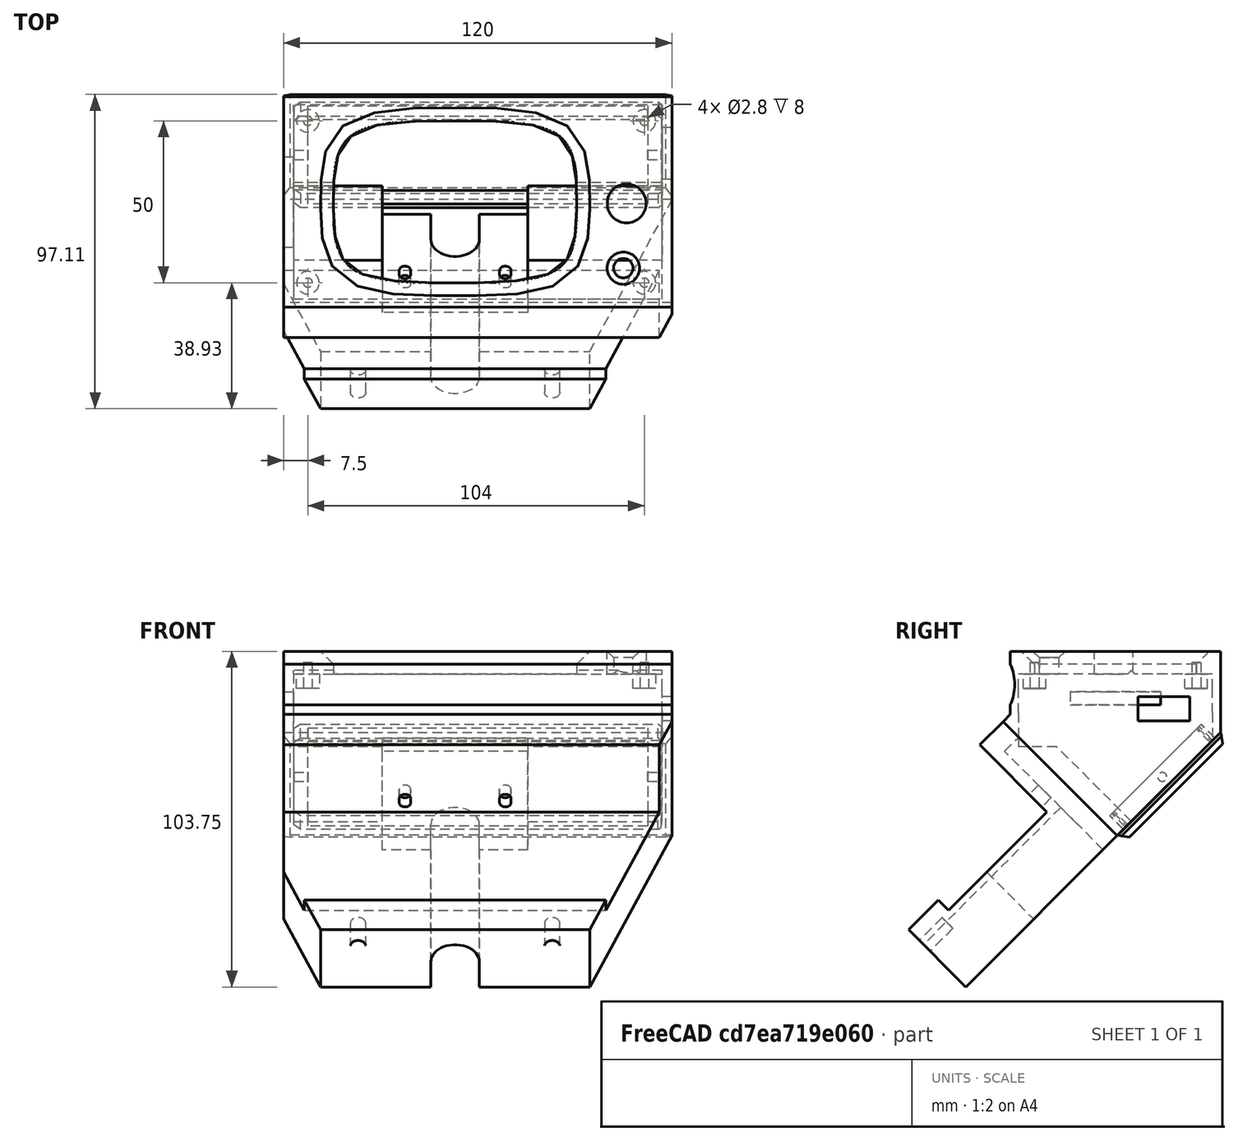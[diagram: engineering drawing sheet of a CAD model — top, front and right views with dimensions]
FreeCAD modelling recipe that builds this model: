
FCSTD DOCUMENT  (FreeCAD 0.19R)
Label: ScreenBezel2
License: All rights reserved
LicenseURL: http://en.wikipedia.org/wiki/All_rights_reserved
objects: Sketcher::SketchObject×24, PartDesign::Pocket×19, PartDesign::Chamfer×7, PartDesign::Pad×5, PartDesign::Body×2, PartDesign::Mirrored×1, Mesh::Feature×1
note: 89 computed .brp shape members not serialized (recipe doc carries the construction recipe); baked Part::Feature solids carry a one-line shape summary decoded from their .brp

FEATURE [Sketcher::SketchObject] Sketch
  FullyConstrained = true
  MapMode = 5
  Support = -> [XY_Plane]
  sketch-geometry (30):
    g0: LineSegment StartX=-53 StartY=32.5 StartZ=0 EndX=67 EndY=32.5 EndZ=0
    g1: LineSegment StartX=67 StartY=32.5 StartZ=0 EndX=67 EndY=-32.5 EndZ=0
    g2: LineSegment StartX=67 StartY=-32.5 StartZ=0 EndX=-53 EndY=-32.5 EndZ=0
    g3: LineSegment StartX=-53 StartY=-32.5 StartZ=0 EndX=-53 EndY=32.5 EndZ=0
    g4: LineSegment StartX=-37 StartY=24.5 StartZ=0 EndX=37 EndY=24.5 EndZ=0
    g5: LineSegment StartX=37 StartY=24.5 StartZ=0 EndX=37 EndY=-24.5 EndZ=0
    g6: LineSegment StartX=37 StartY=-24.5 StartZ=0 EndX=-37 EndY=-24.5 EndZ=0
    g7: LineSegment StartX=-37 StartY=-24.5 StartZ=0 EndX=-37 EndY=24.5 EndZ=0
    g8: LineSegment StartX=-37.7408 StartY=25.116 StartZ=0 EndX=37.7408 EndY=25.116 EndZ=0
    g9: LineSegment StartX=37.7408 StartY=25.116 StartZ=0 EndX=37.7408 EndY=-25.116 EndZ=0
    g10: LineSegment StartX=37.7408 StartY=-25.116 StartZ=0 EndX=-37.7408 EndY=-25.116 EndZ=0
    g11: LineSegment StartX=-37.7408 StartY=-25.116 StartZ=0 EndX=-37.7408 EndY=25.116 EndZ=0
    g12-g19: Circle x8 (B-spline internal-alignment scaffolding for g20; pole/knot coordinates omitted)
    g20: BSplineCurve PolesCount=8 KnotsCount=9 Degree=3 IsPeriodic=1
    g21-g29: GeomPoint x9 (B-spline internal-alignment scaffolding for g20; pole/knot coordinates omitted)
  constraints (53):
    c: Coincident(g0,g1)
    c: Coincident(g1,g2)
    c: Coincident(g2,g3)
    c: Coincident(g3,g0)
    c: Horizontal(g0)
    c: Horizontal(g2)
    c: Vertical(g1)
    c: Vertical(g3)
    c: Coincident(g4,g5)
    c: Coincident(g5,g6)
    c: Coincident(g6,g7)
    c: Coincident(g7,g4)
    c: Horizontal(g4)
    c: Vertical(g7)
    c: Distance(g5) = 49
    c: Distance(g4,g3) = 16
    c: Distance(g0,g5) = 30
    c: Distance(g6,g2) = 8
    c: Distance(g4,g0) = 8
    c: Distance(g6) = 74
    c: Symmetric(g5,g6,g-2)
    c: Symmetric(g5,g4,g-1)
    c: Coincident(g8,g9)
    c: Coincident(g9,g10)
    c: Coincident(g10,g11)
    c: Coincident(g11,g8)
    c: Horizontal(g8)
    c: Horizontal(g10)
    c: Vertical(g9)
    c: Vertical(g11)
    c: Symmetric(g9,g8,g-1)
    c: Weight(g12) = 1
    c: Equal(g12,g13)
    c: Equal(g12,g14)
    c: Equal(g12,g15)
    c: PointOnObject(g15,g-1)
    c: Equal(g12,g16)
    c: Equal(g12,g17)
    c: PointOnObject(g17,g-2)
    c: Equal(g12,g18)
    c: Equal(g12,g19)
    c: InternalAlignment(g12-g19 -> g20) x8
    c: InternalAlignment(g21-g29 -> g20) x9
    c: Coincident(g8,g12)
    c: Coincident(g14,g8)
    c: Coincident(g16,g10)
    c: Coincident(g18,g9)
    c: Distance(g19,g5) = 0.5
    c: Symmetric(g19,g15,g-2)
    c: Distance(g17,g6) = 0.5
    c: Symmetric(g17,g13,g-1)
    c: DistanceX(g8) = 37.7408
    c: DistanceY(g8) = 25.116
FEATURE [PartDesign::Pad] Pad
  Direction = (1,1,1)
  Length = 25
  Length2 = 100
  Profile = -> Sketch
  Type = 0
FEATURE [Sketcher::SketchObject] Sketch004  label="knob"
  FullyConstrained = false
  MapMode = 5
  Placement = pos=(0,0,0) rot=(1,0,0;3.14159rad)
  sketch-geometry (1):
    g0: Circle CenterX=52 CenterY=20.5 CenterZ=0 NormalX=0 NormalY=0 NormalZ=1 AngleXU=0 Radius=3
  constraints (1):
    c: Diameter(g0) = 6
FEATURE [PartDesign::Pocket] Pocket001
  BaseFeature = -> Pad
  Length = 5
  Length2 = 100
  Profile = -> Sketch004
  Type = 1
FEATURE [Sketcher::SketchObject] Sketch001  label="knob001"
  FullyConstrained = false
  MapMode = 5
  Placement = pos=(0,0,25) rot=(0,0,1;0rad)
  Support = -> [Pocket001]
  sketch-geometry (1):
    g0: Circle CenterX=53 CenterY=-0.5 CenterZ=0 NormalX=0 NormalY=0 NormalZ=1 AngleXU=0 Radius=6
  constraints (2):
    c: Diameter(g0) = 12
    c: DistanceY(g0) = -0.5
FEATURE [PartDesign::Pocket] Pocket
  BaseFeature = -> Pocket001
  Length = 5
  Length2 = 100
  Profile = -> Sketch001
  Type = 1
FEATURE [Sketcher::SketchObject] Sketch005  label="MainPCBPocket"
  FullyConstrained = true
  MapMode = 5
  Placement = pos=(0,0,0) rot=(1,0,0;3.14159rad)
  Support = -> [Pocket]
  sketch-geometry (4):
    g0: LineSegment StartX=-50 StartY=30 StartZ=0 EndX=64 EndY=30 EndZ=0
    g1: LineSegment StartX=64 StartY=30 StartZ=0 EndX=64 EndY=-30 EndZ=0
    g2: LineSegment StartX=64 StartY=-30 StartZ=0 EndX=-50 EndY=-30 EndZ=0
    g3: LineSegment StartX=-50 StartY=-30 StartZ=0 EndX=-50 EndY=30 EndZ=0
  constraints (11):
    c: Coincident(g0,g1)
    c: Coincident(g1,g2)
    c: Coincident(g2,g3)
    c: Coincident(g3,g0)
    c: Horizontal(g0)
    c: Horizontal(g2)
    c: Vertical(g1)
    c: Symmetric(g2,g0,g-1)
    c: DistanceX(g0) = -50
    c: DistanceY(g0) = 30
    c: DistanceX(g1) = 64
FEATURE [PartDesign::Pocket] Pocket002
  BaseFeature = -> Pocket
  Length = 18
  Length2 = 100
  Profile = -> Sketch005
  Type = 0
FEATURE [PartDesign::Chamfer] Chamfer
  Angle = 45
  Base = -> Pocket002 [Edge19]
  BaseFeature = -> Pocket002
  ChamferType = 0
  FlipDirection = false
  Size = 4
  Size2 = 1
  SupportTransform = false
FEATURE [Sketcher::SketchObject] Sketch006  label="standofs"
  FullyConstrained = true
  MapMode = 5
  Placement = pos=(0,0,18) rot=(1,0,0;3.14159rad)
  Support = -> [Chamfer]
  sketch-geometry (4):
    g0: Circle CenterX=-45.5 CenterY=25 CenterZ=0 NormalX=0 NormalY=0 NormalZ=1 AngleXU=0 Radius=3.5
    g1: Circle CenterX=-45.5 CenterY=-25 CenterZ=0 NormalX=0 NormalY=0 NormalZ=1 AngleXU=0 Radius=3.5
    g2: Circle CenterX=58.5 CenterY=-25 CenterZ=0 NormalX=0 NormalY=0 NormalZ=1 AngleXU=0 Radius=3.5
    g3: Circle CenterX=58.5 CenterY=25 CenterZ=0 NormalX=0 NormalY=0 NormalZ=1 AngleXU=0 Radius=3.5
  constraints (10):
    c: Diameter(g0) = 7
    c: Equal(g0,g1)
    c: Equal(g0,g3)
    c: Equal(g0,g2)
    c: Symmetric(g1,g0,g-1)
    c: Symmetric(g2,g3,g-1)
    c: Distance(g3,g2) = 50
    c: Distance(g1,g0) = 50
    c: Distance(g3,g0) = 104
    c: DistanceX(g0) = -45.5
FEATURE [PartDesign::Pad] Pad001
  BaseFeature = -> Chamfer
  Direction = (1,1,1)
  Length = 4.5
  Length2 = 100
  Profile = -> Sketch006
  Type = 0
FEATURE [Sketcher::SketchObject] Sketch007  label="holes"
  FullyConstrained = true
  MapMode = 5
  Placement = pos=(0,0,13.5) rot=(1,0,0;3.14159rad)
  Support = -> [Pad001]
  sketch-geometry (4):
    g0: Circle CenterX=-45.5 CenterY=25 CenterZ=0 NormalX=0 NormalY=0 NormalZ=1 AngleXU=0 Radius=1.4
    g1: Circle CenterX=58.5 CenterY=25 CenterZ=0 NormalX=0 NormalY=0 NormalZ=1 AngleXU=0 Radius=1.4
    g2: Circle CenterX=58.5 CenterY=-25 CenterZ=0 NormalX=0 NormalY=0 NormalZ=1 AngleXU=0 Radius=1.4
    g3: Circle CenterX=-45.5 CenterY=-25 CenterZ=0 NormalX=0 NormalY=0 NormalZ=1 AngleXU=0 Radius=1.4
  constraints (10):
    c: Distance(g3,g2) = 104
    c: Distance(g3,g0) = 50
    c: Symmetric(g3,g0,g-1)
    c: Symmetric(g2,g1,g-1)
    c: Diameter(g1) = 2.8
    c: Equal(g1,g2)
    c: Equal(g1,g3)
    c: Equal(g1,g0)
    c: DistanceX(g0) = -45.5
    c: Distance(g1,g2) = 50
FEATURE [PartDesign::Pocket] Pocket003
  BaseFeature = -> Pad001
  Length = 8
  Length2 = 100
  Profile = -> Sketch007
  Type = 0
FEATURE [Sketcher::SketchObject] Sketch008  label="USBhole"
  ExternalGeometry = -> [Pocket003]
  FullyConstrained = true
  MapMode = 5
  Placement = pos=(67,0,0) rot=(0.57735,0.57735,0.57735;2.0944rad)
  Support = -> [Pocket003]
  sketch-geometry (4):
    g0: LineSegment StartX=7 StartY=6.5 StartZ=0 EndX=23 EndY=6.5 EndZ=0
    g1: LineSegment StartX=23 StartY=6.5 StartZ=0 EndX=23 EndY=0 EndZ=0
    g2: LineSegment StartX=23 StartY=0 StartZ=0 EndX=7 EndY=0 EndZ=0
    g3: LineSegment StartX=7 StartY=0 StartZ=0 EndX=7 EndY=6.5 EndZ=0
  constraints (12):
    c: Coincident(g0,g1)
    c: Coincident(g1,g2)
    c: Coincident(g2,g3)
    c: Coincident(g3,g0)
    c: Horizontal(g0)
    c: Horizontal(g2)
    c: Vertical(g1)
    c: Vertical(g3)
    c: Distance(g-3,g0) = 7
    c: Distance(g0) = 16
    c: Distance(g0,g-4) = 7
    c: PointOnObject(g1,g-1)
FEATURE [PartDesign::Pocket] Pocket004
  BaseFeature = -> Pocket003
  Length = 9
  Length2 = 100
  Profile = -> Sketch008
  Type = 0
FEATURE [Sketcher::SketchObject] Sketch009  label="SDHole"
  ExternalGeometry = -> [Pocket004]
  FullyConstrained = true
  MapMode = 5
  Placement = pos=(-53,0,0) rot=(0.57735,-0.57735,-0.57735;2.0944rad)
  Support = -> [Pocket004]
  sketch-geometry (4):
    g0: LineSegment StartX=-14 StartY=12.5 StartZ=0 EndX=14 EndY=12.5 EndZ=0
    g1: LineSegment StartX=14 StartY=12.5 StartZ=0 EndX=14 EndY=8.5 EndZ=0
    g2: LineSegment StartX=14 StartY=8.5 StartZ=0 EndX=-14 EndY=8.5 EndZ=0
    g3: LineSegment StartX=-14 StartY=8.5 StartZ=0 EndX=-14 EndY=12.5 EndZ=0
  constraints (11):
    c: Coincident(g0,g1)
    c: Coincident(g1,g2)
    c: Coincident(g2,g3)
    c: Coincident(g3,g0)
    c: Horizontal(g0)
    c: Vertical(g1)
    c: Vertical(g3)
    c: Distance(g0,g-3) = 1
    c: Distance(g1) = 4
    c: Symmetric(g1,g2,g-2)
    c: Distance(g2) = 28
FEATURE [PartDesign::Pocket] Pocket005
  BaseFeature = -> Pocket004
  Length = 5
  Length2 = 100
  Profile = -> Sketch009
  Type = 0
FEATURE [Sketcher::SketchObject] Sketch010  label="TowerProper"
  FullyConstrained = false
  MapMode = 5
  Placement = pos=(-53,0,0) rot=(0.57735,-0.57735,-0.57735;2.0944rad)
  Support = -> [Pocket005]
  sketch-geometry (6):
    g0: LineSegment StartX=-32.5 StartY=0 StartZ=0 EndX=46.2475 EndY=-78.7475 EndZ=0
    g1: LineSegment StartX=46.2475 StartY=-78.7475 StartZ=0 EndX=81.4975 EndY=-43.4975 EndZ=0
    g2: LineSegment StartX=81.4975 StartY=-43.4975 StartZ=0 EndX=32 EndY=6 EndZ=0
    g3: LineSegment StartX=-0.680195 StartY=-31.8198 StartZ=0 EndX=-60.5279 EndY=28.0279 EndZ=0
    g4: LineSegment StartX=32 StartY=6 StartZ=0 EndX=-32.5 EndY=6 EndZ=0
    g5: LineSegment StartX=-32.5 StartY=6 StartZ=0 EndX=-32.5 EndY=0 EndZ=0
  constraints (15):
    c: Coincident(g0,g1)
    c: Coincident(g1,g2)
    c: Parallel(g0,g2)
    c: Perpendicular(g0,g1)
    c: PointOnObject(g5,g-1)
    c: Coincident(g4,g2)
    c: Horizontal(g4)
    c: DistanceX(g4) = -32.5
    c: Coincident(g5,g4)
    c: Vertical(g5)
    c: DistanceY(g4) = 6
    c: DistanceX(g2) = 32
    c: Coincident(g0,g5)
    c: Angle(g0) = -0.785398
    c: Distance(g2) = 70
FEATURE [PartDesign::Pad] Pad002  label="Backbit"
  BaseFeature = -> Pocket005
  Direction = (1,1,1)
  Length = 120
  Length2 = 100
  Profile = -> Sketch010
  Reversed = true
  Type = 0
FEATURE [Sketcher::SketchObject] Sketch015  label="hollowOutPocket"
  FullyConstrained = true
  MapMode = 5
  Placement = pos=(0,0,13.5) rot=(1,0,0;3.14159rad)
  sketch-geometry (4):
    g0: LineSegment StartX=-50 StartY=30 StartZ=0 EndX=64 EndY=30 EndZ=0
    g1: LineSegment StartX=64 StartY=30 StartZ=0 EndX=64 EndY=-30 EndZ=0
    g2: LineSegment StartX=64 StartY=-30 StartZ=0 EndX=-50 EndY=-30 EndZ=0
    g3: LineSegment StartX=-50 StartY=-30 StartZ=0 EndX=-50 EndY=30 EndZ=0
  constraints (11):
    c: Coincident(g0,g1)
    c: Coincident(g1,g2)
    c: Coincident(g2,g3)
    c: Coincident(g3,g0)
    c: Horizontal(g0)
    c: Horizontal(g2)
    c: Vertical(g1)
    c: DistanceX(g0) = 64
    c: DistanceX(g0) = -50
    c: Distance(g3) = 60
    c: Symmetric(g2,g0,g-1)
FEATURE [PartDesign::Pocket] Pocket006
  BaseFeature = -> Pad002
  Length = 18
  Length2 = 100
  Profile = -> Sketch015
  Reversed = true
  Type = 0
FEATURE [Sketcher::SketchObject] Sketch016  label="UsbRetrim"
  FullyConstrained = true
  MapMode = 5
  Placement = pos=(67,0,0) rot=(0.57735,0.57735,0.57735;2.0944rad)
  Support = -> [Pocket006]
  sketch-geometry (4):
    g0: LineSegment StartX=7 StartY=11 StartZ=0 EndX=23 EndY=11 EndZ=0
    g1: LineSegment StartX=23 StartY=11 StartZ=0 EndX=23 EndY=3.5 EndZ=0
    g2: LineSegment StartX=23 StartY=3.5 StartZ=0 EndX=7 EndY=3.5 EndZ=0
    g3: LineSegment StartX=7 StartY=3.5 StartZ=0 EndX=7 EndY=11 EndZ=0
  constraints (12):
    c: Coincident(g0,g1)
    c: Coincident(g1,g2)
    c: Coincident(g2,g3)
    c: Coincident(g3,g0)
    c: Horizontal(g0)
    c: Horizontal(g2)
    c: Vertical(g1)
    c: Vertical(g3)
    c: Distance(g1) = 7.5
    c: Distance(g2) = 16
    c: DistanceX(g0) = 7
    c: DistanceY(g0) = 11
FEATURE [PartDesign::Pocket] Pocket007
  BaseFeature = -> Pocket006
  Length = 9
  Length2 = 100
  Profile = -> Sketch016
  Type = 0
FEATURE [PartDesign::Chamfer] Chamfer001
  Angle = 45
  Base = -> Pocket007 [Edge6]
  BaseFeature = -> Pocket007
  ChamferType = 0
  FlipDirection = false
  Size = 2
  Size2 = 1
  SupportTransform = false
FEATURE [Sketcher::SketchObject] Sketch018
  FullyConstrained = true
  MapMode = 5
  Placement = pos=(0,0,0) rot=(1,0,0;1.5708rad)
  Support = -> [XZ_Plane001]
  sketch-geometry (4):
    g0: LineSegment StartX=-60 StartY=22.5 StartZ=0 EndX=60 EndY=22.5 EndZ=0
    g1: LineSegment StartX=60 StartY=22.5 StartZ=0 EndX=60 EndY=-22.5 EndZ=0
    g2: LineSegment StartX=60 StartY=-22.5 StartZ=0 EndX=-60 EndY=-22.5 EndZ=0
    g3: LineSegment StartX=-60 StartY=-22.5 StartZ=0 EndX=-60 EndY=22.5 EndZ=0
  constraints (10):
    c: Coincident(g0,g1)
    c: Coincident(g1,g2)
    c: Coincident(g2,g3)
    c: Coincident(g3,g0)
    c: Horizontal(g2)
    c: Vertical(g3)
    c: Symmetric(g0,g0,g-2)
    c: Distance(g0) = 120
    c: Distance(g1) = 45
    c: Symmetric(g1,g0,g-1)
FEATURE [PartDesign::Pad] Pad003
  Direction = (1,1,1)
  Length = 3
  Length2 = 100
  Placement = pos=(0,0,0) rot=(1,0,0;1.5708rad)
  Profile = -> Sketch018
  Type = 0
FEATURE [Sketcher::SketchObject] Sketch019
  FullyConstrained = true
  MapMode = 5
  Placement = pos=(0,-3,7e-16) rot=(1,0,0;1.5708rad)
  Support = -> [Pad003]
  sketch-geometry (4):
    g0: LineSegment StartX=-56.75 StartY=20 StartZ=0 EndX=56.75 EndY=20 EndZ=0
    g1: LineSegment StartX=56.75 StartY=20 StartZ=0 EndX=56.75 EndY=-20 EndZ=0
    g2: LineSegment StartX=56.75 StartY=-20 StartZ=0 EndX=-56.75 EndY=-20 EndZ=0
    g3: LineSegment StartX=-56.75 StartY=-20 StartZ=0 EndX=-56.75 EndY=20 EndZ=0
  constraints (11):
    c: Coincident(g0,g1)
    c: Coincident(g1,g2)
    c: Coincident(g2,g3)
    c: Coincident(g3,g0)
    c: Horizontal(g0)
    c: Horizontal(g2)
    c: Vertical(g1)
    c: Vertical(g3)
    c: Distance(g0) = 113.5
    c: Distance(g1) = 40
    c: Symmetric(g1,g0,g-1)
FEATURE [PartDesign::Pad] Pad004
  BaseFeature = -> Pad003
  Direction = (1,1,1)
  Length = 6
  Length2 = 100
  Placement = pos=(0,0,0) rot=(1,0,0;1.5708rad)
  Profile = -> Sketch019
  Type = 0
FEATURE [Sketcher::SketchObject] Sketch020
  FullyConstrained = true
  MapMode = 5
  Placement = pos=(56.75,0,0) rot=(0.707107,0,0.707107;3.14159rad)
  Support = -> [Pad004]
  sketch-geometry (1):
    g0: Circle CenterX=0 CenterY=6 CenterZ=0 NormalX=0 NormalY=0 NormalZ=1 AngleXU=0 Radius=1.4
  constraints (3):
    c: PointOnObject(g0,g-2)
    c: Diameter(g0) = 2.8
    c: DistanceY(g0) = 6
FEATURE [PartDesign::Pocket] Pocket008
  BaseFeature = -> Pad004
  Length = 5
  Length2 = 100
  Placement = pos=(0,0,0) rot=(1,0,0;1.5708rad)
  Profile = -> Sketch020
  Type = 1
FEATURE [Sketcher::SketchObject] Sketch021
  FullyConstrained = true
  MapMode = 5
  Placement = pos=(0,-9,1.5e-14) rot=(1,0,0;1.5708rad)
  sketch-geometry (4):
    g0: LineSegment StartX=-52.5 StartY=18.5 StartZ=0 EndX=52.5 EndY=18.5 EndZ=0
    g1: LineSegment StartX=52.5 StartY=18.5 StartZ=0 EndX=52.5 EndY=-18.5 EndZ=0
    g2: LineSegment StartX=52.5 StartY=-18.5 StartZ=0 EndX=-52.5 EndY=-18.5 EndZ=0
    g3: LineSegment StartX=-52.5 StartY=-18.5 StartZ=0 EndX=-52.5 EndY=18.5 EndZ=0
  constraints (11):
    c: Coincident(g0,g1)
    c: Coincident(g1,g2)
    c: Coincident(g2,g3)
    c: Coincident(g3,g0)
    c: Horizontal(g0)
    c: Horizontal(g2)
    c: Vertical(g1)
    c: Vertical(g3)
    c: Distance(g0) = 105
    c: Symmetric(g0,g2,g-1)
    c: Distance(g1) = 37
FEATURE [Sketcher::SketchObject] Sketch024
  ExternalGeometry = -> [Pocket008]
  FullyConstrained = false
  MapMode = 5
  Placement = pos=(60,0,0) rot=(0.707107,0,0.707107;3.14159rad)
  Support = -> [Pocket008]
  sketch-geometry (3):
    g0: LineSegment StartX=-22.5 StartY=3 StartZ=0 EndX=-17.8755 EndY=-3.60453 EndZ=0
    g1: LineSegment StartX=-17.8755 StartY=-3.60453 StartZ=0 EndX=-35.5163 EndY=-3.60453 EndZ=0
    g2: LineSegment StartX=-35.5163 StartY=-3.60453 StartZ=0 EndX=-22.5 EndY=3 EndZ=0
  constraints (6):
    c: Coincident(g0,g1)
    c: Horizontal(g1)
    c: Coincident(g1,g2)
    c: Coincident(g2,g0)
    c: Angle(g0) = -0.959931
    c: Coincident(g0,g-3)
FEATURE [PartDesign::Pocket] Pocket012
  BaseFeature = -> Pocket008
  Length = 5
  Length2 = 100
  Placement = pos=(0,0,0) rot=(1,0,0;1.5708rad)
  Profile = -> Sketch024
  Type = 1
FEATURE [PartDesign::Mirrored] Mirrored
  BaseFeature = -> Pocket012
  MirrorPlane = -> Sketch024 [V_Axis]
  Originals = -> [Pocket012]
  Placement = pos=(0,0,0) rot=(1,0,0;1.5708rad)
FEATURE [PartDesign::Chamfer] Chamfer008
  Angle = 45
  Base = -> Mirrored [Edge14,Edge12]
  BaseFeature = -> Mirrored
  ChamferType = 0
  FlipDirection = false
  Placement = pos=(0,0,0) rot=(1,0,0;1.5708rad)
  Size = 2
  Size2 = 1
  SupportTransform = false
FEATURE [PartDesign::Pocket] Pocket013
  BaseFeature = -> Chamfer008
  Length = 6
  Length2 = 100
  Placement = pos=(0,0,0) rot=(1,0,0;1.5708rad)
  Profile = -> Sketch021
  Type = 0
FEATURE [PartDesign::Chamfer] Chamfer009
  Angle = 45
  Base = -> Pocket013 [Edge29]
  BaseFeature = -> Pocket013
  ChamferType = 0
  FlipDirection = false
  Placement = pos=(0,0,0) rot=(1,0,0;1.5708rad)
  Size = 2
  Size2 = 1
  SupportTransform = false
FEATURE [PartDesign::Chamfer] Chamfer010
  Angle = 45
  Base = -> Chamfer009 [Edge11]
  BaseFeature = -> Chamfer009
  ChamferType = 0
  FlipDirection = false
  Placement = pos=(0,0,0) rot=(1,0,0;1.5708rad)
  Size = 1
  Size2 = 1
  SupportTransform = false
FEATURE [PartDesign::Chamfer] Chamfer011
  Angle = 45
  Base = -> Chamfer010 [Edge18]
  BaseFeature = -> Chamfer010
  ChamferType = 0
  FlipDirection = false
  Placement = pos=(0,0,0) rot=(1,0,0;1.5708rad)
  Size = 1
  Size2 = 1
  SupportTransform = false
FEATURE [PartDesign::Chamfer] Chamfer012
  Angle = 45
  Base = -> Chamfer011 [Edge20]
  BaseFeature = -> Chamfer011
  ChamferType = 0
  FlipDirection = false
  Placement = pos=(0,0,0) rot=(1,0,0;1.5708rad)
  Size = 2
  Size2 = 1
  SupportTransform = false
FEATURE [PartDesign::Body] Body001  label="BoxCap"
  Group = -> [Sketch018,Pad003,Sketch019,Pad004,Sketch020,Pocket008,Sketch021,Sketch024,Pocket012,Mirrored,Chamfer008,Pocket013,Chamfer009,Chamfer010,Chamfer011,Chamfer012]
  Origin = -> Origin001
  Placement = pos=(7,18.751,-18.0573) rot=(-1,0,0;0.785398rad)
  Tip = -> Chamfer012
FEATURE [Sketcher::SketchObject] Sketch033  label="beltPath"
  FullyConstrained = false
  MapMode = 5
  Placement = pos=(-53,0,0) rot=(0.57735,-0.57735,-0.57735;2.0944rad)
  sketch-geometry (6):
    g0: LineSegment StartX=63.9251 StartY=-61.0698 StartZ=0 EndX=54.7328 EndY=-51.8774 EndZ=0
    g1: LineSegment StartX=54.7328 StartY=-51.8774 StartZ=0 EndX=51.5508 EndY=-55.0594 EndZ=0
    g2: LineSegment StartX=51.5508 StartY=-55.0594 StartZ=0 EndX=21.1452 EndY=-24.6538 EndZ=0
    g3: LineSegment StartX=21.1452 StartY=-24.6538 StartZ=0 EndX=72.969 EndY=27.17 EndZ=0
    g4: LineSegment StartX=72.969 StartY=27.17 StartZ=0 EndX=105.178 EndY=-41.8059 EndZ=0
    g5: LineSegment StartX=63.9251 StartY=-61.0698 StartZ=0 EndX=105.178 EndY=-41.8059 EndZ=0
  constraints (16):
    c: Coincident(g1,g0)
    c: Coincident(g2,g1)
    c: Coincident(g3,g2)
    c: Coincident(g4,g3)
    c: Coincident(g5,g0)
    c: Coincident(g5,g4)
    c: Perpendicular(g4,g5)
    c: Distance(g0) = 13
    c: Angle(g2) = 2.35619
    c: Perpendicular(g3,g2)
    c: DistanceX(g0) = 63.9251
    c: DistanceY(g0) = -61.0698
    c: Angle(g1) = -2.35619
    c: Angle(g0) = 2.35619
    c: Distance(g1) = 4.5
    c: Distance(g2) = 43
FEATURE [Sketcher::SketchObject] Sketch034  label="screwslot"
  FullyConstrained = false
  MapMode = 5
  Placement = pos=(0,-62.4975,-62.4975) rot=(1,0,0;2.35619rad)
  sketch-geometry (7):
    g0: ArcOfCircle CenterX=-2e-16 CenterY=-12 CenterZ=0 NormalX=0 NormalY=0 NormalZ=1 AngleXU=0 Radius=7.5 StartAngle=0 EndAngle=3.14159
    g1: LineSegment StartX=7.5 StartY=-33.2436 StartZ=0 EndX=7.5 EndY=-12 EndZ=0
    g2: LineSegment StartX=-7.5 StartY=-33.2436 StartZ=0 EndX=-7.5 EndY=-12 EndZ=0
    g3: LineSegment StartX=7.5 StartY=-33.2436 StartZ=0 EndX=3.29977 EndY=-37.4439 EndZ=0
    g4: LineSegment StartX=3.29977 StartY=-37.4439 StartZ=0 EndX=-3.29977 EndY=-37.4439 EndZ=0
    g5: LineSegment StartX=-3.29977 StartY=-37.4439 StartZ=0 EndX=-7.5 EndY=-33.2436 EndZ=0
    g6: LineSegment StartX=-1.69433 StartY=-29.9439 StartZ=0 EndX=3.32824 EndY=-29.9439 EndZ=0
  constraints (16):
    c: Tangent(g1,g0) = -1.5708
    c: Tangent(g2,g0) = 1.5708
    c: Vertical(g1)
    c: Diameter(g0) = 15
    c: Coincident(g1,g3)
    c: Coincident(g3,g4)
    c: Horizontal(g4)
    c: Coincident(g4,g5)
    c: Coincident(g5,g2)
    c: Distance(g1,g2) = 15
    c: Equal(g3,g5)
    c: Angle(g3) = -2.35619
    c: Symmetric(g1,g2,g-2)
    c: Horizontal(g6)
    c: Distance(g6,g4) = 7.5
    c: DistanceY(g0) = -12
FEATURE [Sketcher::SketchObject] Sketch041  label="ScreenBack"
  FullyConstrained = false
  MapMode = 5
  Placement = pos=(0,16.25,-16.25) rot=(1,0,0;3.92699rad)
  Support = -> [Pocket006]
  sketch-geometry (4):
    g0: LineSegment StartX=-50 StartY=16 StartZ=0 EndX=64 EndY=16 EndZ=0
    g1: LineSegment StartX=64 StartY=16 StartZ=0 EndX=64 EndY=-16.9876 EndZ=0
    g2: LineSegment StartX=64 StartY=-16.9876 StartZ=0 EndX=-50 EndY=-16.9876 EndZ=0
    g3: LineSegment StartX=-50 StartY=-16.9876 StartZ=0 EndX=-50 EndY=16 EndZ=0
  constraints (11):
    c: Coincident(g0,g1)
    c: Coincident(g1,g2)
    c: Coincident(g2,g3)
    c: Coincident(g3,g0)
    c: Horizontal(g0)
    c: Horizontal(g2)
    c: Vertical(g1)
    c: Vertical(g3)
    c: DistanceX(g0) = -50
    c: DistanceX(g0) = 64
    c: DistanceY(g0) = 16
FEATURE [PartDesign::Pocket] Pocket019
  BaseFeature = -> Chamfer001
  Length = 33
  Length2 = 100
  Profile = -> Sketch041
  Type = 0
FEATURE [Sketcher::SketchObject] Sketch031  label="StepperSlot17"
  ExternalGeometry = -> [Chamfer001]
  FullyConstrained = false
  MapMode = 5
  Placement = pos=(0,16.25,-16.25) rot=(1,0,0;3.92699rad)
  Support = -> [Pocket019]
  sketch-geometry (4):
    g0: LineSegment StartX=-22.5 StartY=-18.4454 StartZ=0 EndX=22.5 EndY=-18.4454 EndZ=0
    g1: LineSegment StartX=22.5 StartY=-18.4454 StartZ=0 EndX=22.5 EndY=28.3848 EndZ=0
    g2: LineSegment StartX=22.5 StartY=28.3848 StartZ=0 EndX=-22.5 EndY=28.3848 EndZ=0
    g3: LineSegment StartX=-22.5 StartY=28.3848 StartZ=0 EndX=-22.5 EndY=-18.4454 EndZ=0
  constraints (10):
    c: Coincident(g0,g1)
    c: Coincident(g1,g2)
    c: Coincident(g2,g3)
    c: Coincident(g3,g0)
    c: Horizontal(g0)
    c: Vertical(g1)
    c: Vertical(g3)
    c: Symmetric(g1,g2,g-2)
    c: Distance(g2) = 45
    c: Distance(g1,g-3) = 60
FEATURE [PartDesign::Pocket] Pocket020
  BaseFeature = -> Pocket019
  Length = 43
  Length2 = 100
  Profile = -> Sketch031
  Type = 0
FEATURE [PartDesign::Pocket] Pocket021
  BaseFeature = -> Pocket020
  Length = 5
  Length2 = 100
  Profile = -> Sketch033
  Type = 1
FEATURE [PartDesign::Pocket] Pocket022
  BaseFeature = -> Pocket021
  Length = 62
  Length2 = 100
  Profile = -> Sketch034
  Type = 0
FEATURE [Sketcher::SketchObject] Sketch036  label="Stepper3mm"
  FullyConstrained = false
  MapMode = 5
  Placement = pos=(0,-22.8995,-22.8995) rot=(1,0,0;2.35619rad)
  Support = -> [Pocket022]
  sketch-geometry (21):
    g0: ArcOfCircle CenterX=15.5 CenterY=3.5 CenterZ=0 NormalX=0 NormalY=0 NormalZ=1 AngleXU=0 Radius=1.75 StartAngle=9e-16 EndAngle=3.14159
    g1: ArcOfCircle CenterX=15.5 CenterY=1.5 CenterZ=0 NormalX=0 NormalY=0 NormalZ=1 AngleXU=0 Radius=1.75 StartAngle=3.14159 EndAngle=6.28319
    g2: LineSegment StartX=13.75 StartY=3.5 StartZ=0 EndX=13.75 EndY=1.5 EndZ=0
    g3: LineSegment StartX=17.25 StartY=3.5 StartZ=0 EndX=17.25 EndY=1.5 EndZ=0
    g4: ArcOfCircle CenterX=-15.5 CenterY=3.5 CenterZ=0 NormalX=0 NormalY=0 NormalZ=1 AngleXU=0 Radius=1.75 StartAngle=1e-16 EndAngle=3.14159
    g5: ArcOfCircle CenterX=-15.5 CenterY=1.5 CenterZ=0 NormalX=0 NormalY=0 NormalZ=1 AngleXU=0 Radius=1.75 StartAngle=3.14159 EndAngle=6.28319
    g6: LineSegment StartX=-17.25 StartY=3.5 StartZ=0 EndX=-17.25 EndY=1.5 EndZ=0
    g7: LineSegment StartX=-13.75 StartY=3.5 StartZ=0 EndX=-13.75 EndY=1.5 EndZ=0
    g8: ArcOfCircle CenterX=-15.5 CenterY=-27.5 CenterZ=0 NormalX=0 NormalY=0 NormalZ=1 AngleXU=0 Radius=1.75 StartAngle=0 EndAngle=3.14159
    g9: ArcOfCircle CenterX=-15.5 CenterY=-29.5 CenterZ=0 NormalX=0 NormalY=0 NormalZ=1 AngleXU=0 Radius=1.75 StartAngle=3.14159 EndAngle=6.28319
    g10: LineSegment StartX=-17.25 StartY=-27.5 StartZ=0 EndX=-17.25 EndY=-29.5 EndZ=0
    g11: LineSegment StartX=-13.75 StartY=-27.5 StartZ=0 EndX=-13.75 EndY=-29.5 EndZ=0
    g12: ArcOfCircle CenterX=15.5 CenterY=-27.5 CenterZ=0 NormalX=0 NormalY=0 NormalZ=1 AngleXU=0 Radius=1.75 StartAngle=3e-16 EndAngle=3.14159
    g13: ArcOfCircle CenterX=15.5 CenterY=-29.5 CenterZ=0 NormalX=0 NormalY=0 NormalZ=1 AngleXU=0 Radius=1.75 StartAngle=3.14159 EndAngle=6.28319
    g14: LineSegment StartX=13.75 StartY=-27.5 StartZ=0 EndX=13.75 EndY=-29.5 EndZ=0
    g15: LineSegment StartX=17.25 StartY=-27.5 StartZ=0 EndX=17.25 EndY=-29.5 EndZ=0
    g16: LineSegment StartX=-15.5 StartY=3.5 StartZ=0 EndX=15.5 EndY=3.5 EndZ=0
    g17: LineSegment StartX=15.5 StartY=3.5 StartZ=0 EndX=15.5 EndY=-27.5 EndZ=0
    g18: LineSegment StartX=15.5 StartY=-27.5 StartZ=0 EndX=-15.5 EndY=-27.5 EndZ=0
    g19: LineSegment StartX=-15.5 StartY=-27.5 StartZ=0 EndX=-15.5 EndY=3.5 EndZ=0
    g20: Circle CenterX=-2e-16 CenterY=-12 CenterZ=0 NormalX=0 NormalY=0 NormalZ=1 AngleXU=0 Radius=3.20765
  constraints (48):
    c: Tangent(g0,g3) = 1.5708
    c: Tangent(g0,g2) = -1.5708
    c: Tangent(g2,g1) = -1.5708
    c: Tangent(g3,g1) = 1.5708
    c: Vertical(g2)
    c: Equal(g0,g1)
    c: Tangent(g4,g7) = 1.5708
    c: Tangent(g4,g6) = -1.5708
    c: Tangent(g6,g5) = -1.5708
    c: Tangent(g7,g5) = 1.5708
    c: Vertical(g6)
    c: Equal(g4,g5)
    c: Tangent(g8,g11) = 1.5708
    c: Tangent(g8,g10) = -1.5708
    c: Tangent(g10,g9) = -1.5708
    c: Tangent(g11,g9) = 1.5708
    c: Vertical(g10)
    c: Equal(g8,g9)
    c: Tangent(g12,g15) = 1.5708
    c: Tangent(g12,g14) = -1.5708
    c: Tangent(g14,g13) = -1.5708
    c: Tangent(g15,g13) = 1.5708
    c: Vertical(g14)
    c: Equal(g12,g13)
    c: Coincident(g16,g4)
    c: Coincident(g16,g0)
    c: Coincident(g16,g17)
    c: Coincident(g17,g12)
    c: Coincident(g17,g18)
    c: Coincident(g18,g8)
    c: Coincident(g18,g19)
    c: Coincident(g19,g16)
    c: Equal(g19,g16)
    c: Equal(g16,g18)
    c: Equal(g18,g17)
    c: Diameter(g4) = 3.5
    c: Equal(g4,g0)
    c: Equal(g4,g12)
    c: Equal(g4,g8)
    c: Equal(g7,g3)
    c: Equal(g3,g15)
    c: Equal(g15,g11)
    c: Distance(g7) = 2
    c: Distance(g17) = 31
    c: Symmetric(g0,g4,g-2)
    c: Symmetric(g0,g8,g20)
    c: Vertical(g17)
    c: DistanceY(g20) = -12
FEATURE [PartDesign::Pocket] Pocket023
  BaseFeature = -> Pocket022
  Length = 5
  Length2 = 100
  Profile = -> Sketch036
  Type = 0
FEATURE [Sketcher::SketchObject] Sketch042  label="MountHoles"
  ExternalGeometry = -> [Pocket023]
  FullyConstrained = false
  MapMode = 5
  Placement = pos=(0,-62.4975,-62.4975) rot=(1,0,0;2.35619rad)
  Support = -> [Pocket023]
  sketch-geometry (3):
    g0: Circle CenterX=-30 CenterY=-5 CenterZ=0 NormalX=0 NormalY=0 NormalZ=1 AngleXU=0 Radius=2.35
    g1: Circle CenterX=30 CenterY=-5 CenterZ=0 NormalX=0 NormalY=0 NormalZ=1 AngleXU=0 Radius=2.35
    g2: LineSegment StartX=0 StartY=4.11612 StartZ=0 EndX=0 EndY=-8.94769 EndZ=0
  constraints (7):
    c: Distance(g0,g1) = 60
    c: DistanceY(g1) = -5
    c: DistanceY(g0) = -5
    c: Diameter(g0) = 4.7
    c: Equal(g0,g1)
    c: Symmetric(g0,g1,g2)
    c: DistanceX(g2) = 0
FEATURE [PartDesign::Pocket] Pocket024
  BaseFeature = -> Pocket023
  Length = 10
  Length2 = 100
  Profile = -> Sketch042
  Type = 0
FEATURE [Sketcher::SketchObject] Sketch043
  FullyConstrained = true
  MapMode = 5
  Placement = pos=(-53,0,0) rot=(0.57735,-0.57735,-0.57735;2.0944rad)
  Support = -> [Pocket024]
  sketch-geometry (1):
    g0: Circle CenterX=46.1075 CenterY=14.7465 CenterZ=0 NormalX=0 NormalY=0 NormalZ=1 AngleXU=0 Radius=15
  constraints (3):
    c: Diameter(g0) = 30
    c: DistanceX(g0) = 46.1075
    c: DistanceY(g0) = 14.7465
FEATURE [PartDesign::Pocket] Pocket025
  BaseFeature = -> Pocket024
  Length = 5
  Length2 = 100
  Profile = -> Sketch043
  Type = 1
FEATURE [Sketcher::SketchObject] Sketch044
  FullyConstrained = false
  MapMode = 5
  Placement = pos=(0,1.75431,-1.75431) rot=(1,0,0;0.785398rad)
  Support = -> [Pocket025]
  sketch-geometry (7):
    g0: LineSegment StartX=75.5253 StartY=0 StartZ=0 EndX=35 EndY=-105.599 EndZ=0
    g1: LineSegment StartX=35 StartY=-105.599 StartZ=0 EndX=-35 EndY=-105.599 EndZ=0
    g2: LineSegment StartX=-35 StartY=-105.599 StartZ=0 EndX=-75.5253 EndY=0 EndZ=0
    g3: LineSegment StartX=-75.5253 StartY=0 StartZ=0 EndX=-103.489 EndY=-26.5131 EndZ=0
    g4: LineSegment StartX=-103.489 StartY=-26.5131 StartZ=0 EndX=-83.2306 EndY=-139.493 EndZ=0
    g5: LineSegment StartX=-83.2306 StartY=-139.493 StartZ=0 EndX=94.2253 EndY=-139.493 EndZ=0
    g6: LineSegment StartX=94.2253 StartY=-139.493 StartZ=0 EndX=75.5253 EndY=0 EndZ=0
  constraints (12):
    c: Coincident(g0,g1)
    c: Coincident(g1,g2)
    c: Coincident(g2,g3)
    c: Coincident(g3,g4)
    c: Coincident(g4,g5)
    c: Horizontal(g5)
    c: Coincident(g5,g6)
    c: Coincident(g6,g0)
    c: Symmetric(g0,g1,g-2)
    c: Distance(g1) = 70
    c: PointOnObject(g2,g-1)
    c: Symmetric(g0,g2,g-2)
FEATURE [PartDesign::Pocket] Pocket026
  BaseFeature = -> Pocket025
  Length = 34
  Length2 = 100
  Profile = -> Sketch044
  Type = 4
FEATURE [PartDesign::Body] Body  label="ScreenBox"
  Group = -> [Sketch,Pad,Sketch001,Sketch004,Pocket001,Pocket,Sketch005,Pocket002,Chamfer,Sketch006,Pad001,Sketch007,Pocket003,Sketch008,Pocket004,Sketch009,Pocket005,Sketch010,Pad002,Sketch015,Pocket006,Sketch016,Pocket007,Chamfer001,Sketch031,Sketch033,Sketch034,Sketch036,Sketch041,Pocket019,Pocket020,Pocket021,Pocket022,Pocket023,Sketch042,Pocket024,Sketch043,Pocket025,Sketch044,Pocket026]
  Origin = -> Origin
  Tip = -> Pocket026
FEATURE [Mesh::Feature] Mesh  label="Pocket026 (Meshed)"
